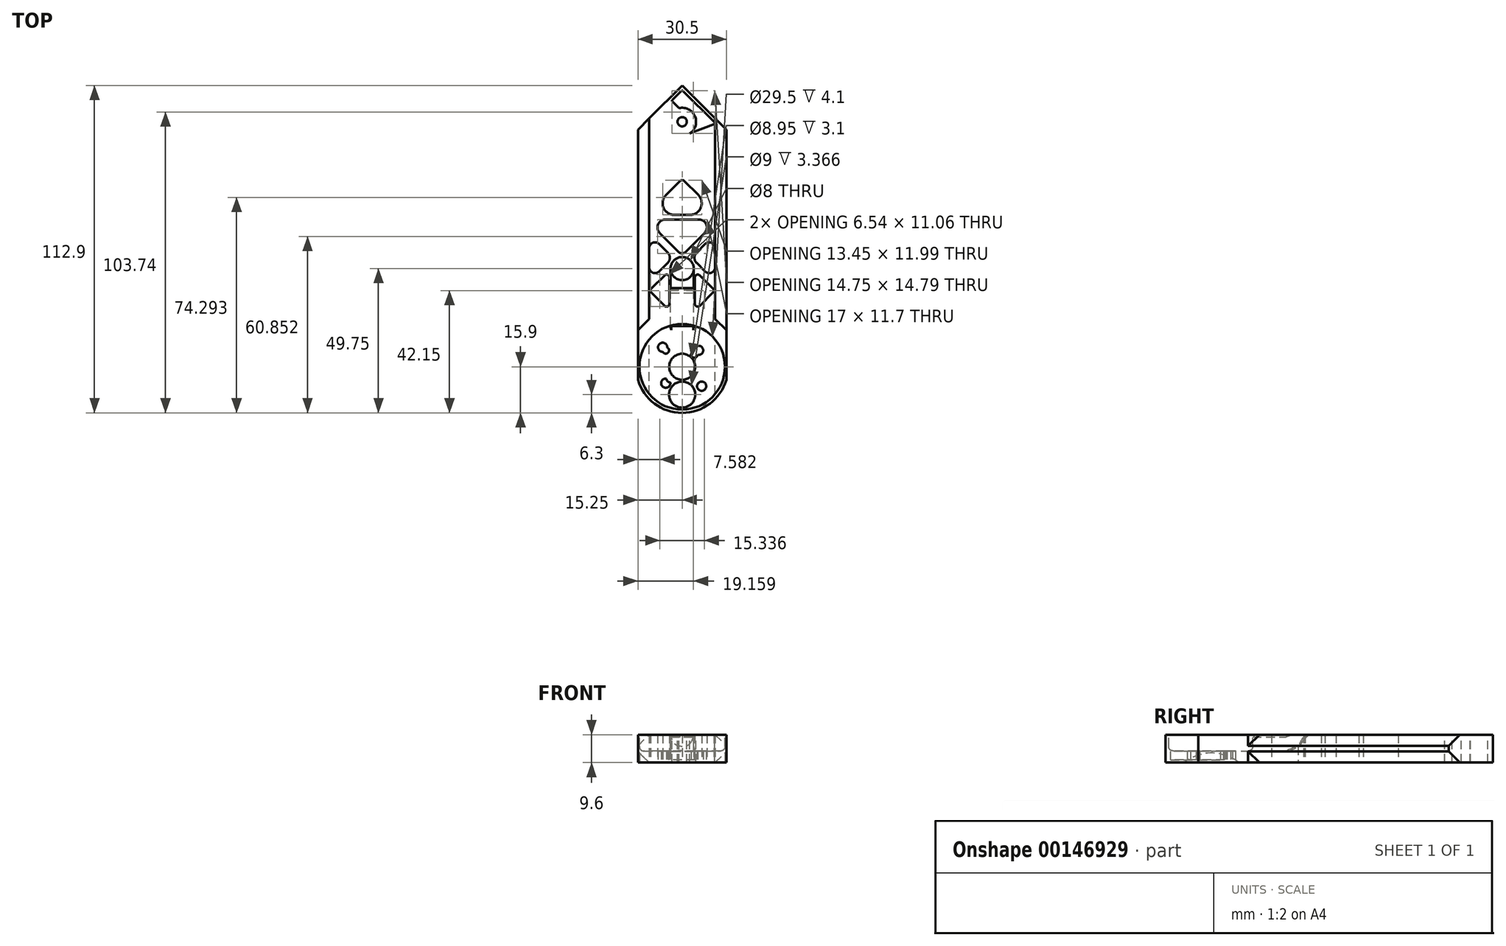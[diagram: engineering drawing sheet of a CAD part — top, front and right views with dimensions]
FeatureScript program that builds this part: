
annotation { "Feature Type Name" : "Feature", "Feature Type Description" : "" }
export const myFeature = defineFeature(function(context is Context, id is Id, definition is map)
    precondition{}
    {
        {
            var Q0;
            Q0=qCreatedBy(makeId("Top.planeOp"),FACE);
            var sketch = newSketch(context, id + "F0", { "sketchPlane" : qUnion([Q0])});
            skLineSegment(sketch, "E0", {"start": v(0, 0) * mm, "end": v(-10, 0) * mm});
            skLineSegment(sketch, "E1", {"start": v(-7.84, 7.84) * mm, "end": v(0, 0) * mm});
            skLineSegment(sketch, "E2", {"start": v(-6.78, -6.78) * mm, "end": v(0, 0) * mm});
            skLineSegment(sketch, "E3", {"start": v(0, 0) * mm, "end": v(-5.66, -5.66) * mm});
            skCircle(sketch, "E4", {"center": v(-5.66, -5.66) * mm, "radius": 1.59 * mm});
            skLineSegment(sketch, "E5", {"start": v(0, 0) * mm, "end": v(-6.72, 6.72) * mm});
            skCircle(sketch, "E6", {"center": v(-6.72, 6.72) * mm, "radius": 1.59 * mm});
            skLineSegment(sketch, "E7", {"start": v(0, 0) * mm, "end": v(-5.66, 5.66) * mm});
            skCircle(sketch, "E8", {"center": v(-5.66, 5.66) * mm, "radius": 1.13 * mm});
            skLineSegment(sketch, "E9.MirrorCS", {"start": v(7.84, -7.84) * mm, "end": v(0, 0) * mm});
            skLineSegment(sketch, "E10.MirrorCS", {"start": v(0, 0) * mm, "end": v(5.66, -5.66) * mm});
            skCircle(sketch, "E11.MirrorC", {"center": v(6.72, -6.72) * mm, "radius": 1.59 * mm});
            skCircle(sketch, "E12.MirrorC", {"center": v(5.66, -5.66) * mm, "radius": 1.13 * mm});
            skLineSegment(sketch, "E13.MirrorCS", {"start": v(0, 0) * mm, "end": v(6.72, -6.72) * mm});
            skCircle(sketch, "E14.MirrorC", {"center": v(5.66, 5.66) * mm, "radius": 1.59 * mm});
            skLineSegment(sketch, "E15.MirrorCS", {"start": v(0, 0) * mm, "end": v(5.66, 5.66) * mm});
            skLineSegment(sketch, "E16.MirrorCS", {"start": v(6.78, 6.78) * mm, "end": v(0, 0) * mm});
            skPoint(sketch, "E17.MirrorCS.start.orphan", {"position": v(0, 10) * mm});
            skPoint(sketch, "E18.orphan", {"position": v(10, 10) * mm});
            skPoint(sketch, "E19.orphan", {"position": v(10, -10) * mm});
            skPoint(sketch, "E20.orphan", {"position": v(-10, 10) * mm});
            skPoint(sketch, "E21.orphan", {"position": v(-10, -10) * mm});
            skCircle(sketch, "E22", {"center": v(-4.24, -4.24) * mm, "radius": 1.13 * mm});
            skCircle(sketch, "E23", {"center": v(4.24, 4.24) * mm, "radius": 1.13 * mm});
            skSolve(sketch);
        }
        {
            var Q0;
            Q0=qCreatedBy(makeId("Front.planeOp"),FACE);
            var sketch = newSketch(context, id + "F1", { "sketchPlane" : qUnion([Q0])});
            skLineSegment(sketch, "E24", {"start": v(0, 0) * mm, "end": v(11.35, 0) * mm});
            skLineSegment(sketch, "E25", {"start": v(-11.35, 0) * mm, "end": v(0, 0) * mm});
            skLineSegment(sketch, "E26", {"start": v(0, 0) * mm, "end": v(0, 3.8) * mm});
            skLineSegment(sketch, "E27", {"start": v(0, 3.8) * mm, "end": v(15.25, 3.8) * mm});
            skLineSegment(sketch, "E28", {"start": v(-15.25, 3.8) * mm, "end": v(0, 3.8) * mm});
            skPoint(sketch, "E29.orphan", {"position": v(15.25, 0) * mm});
            skPoint(sketch, "E30.orphan", {"position": v(-15.25, 0) * mm});
            skLineSegment(sketch, "E31", {"start": v(-15.25, 3.8) * mm, "end": v(-11.35, 0) * mm});
            skLineSegment(sketch, "E32", {"start": v(15.25, 3.8) * mm, "end": v(11.35, 0) * mm});
            skLineSegment(sketch, "E33", {"start": v(15.25, 3.8) * mm, "end": v(15.25, 5.8) * mm});
            skLineSegment(sketch, "E34", {"start": v(15.25, 5.8) * mm, "end": v(11.35, 9.6) * mm});
            skLineSegment(sketch, "E35", {"start": v(11.35, 9.6) * mm, "end": v(0, 9.6) * mm});
            skLineSegment(sketch, "E36.MirrorCS", {"start": v(-11.35, 9.6) * mm, "end": v(0, 9.6) * mm});
            skLineSegment(sketch, "E37.MirrorCS", {"start": v(-15.25, 5.8) * mm, "end": v(-11.35, 9.6) * mm});
            skLineSegment(sketch, "E38.MirrorCS", {"start": v(-15.25, 3.8) * mm, "end": v(-15.25, 5.8) * mm});
            skSolve(sketch);
        }
        {
            var Q0;
            Q0=qSketchRegion(id+"F1",true);
            extrude(context, id + "F2", {"entities" : qUnion([Q0]), "depth" : 16.3 * mm, "hasSecondDirection" : true, "secondDirectionOppositeDirection" : true, "secondDirectionDepth" : 97 * mm});
        }
        {
            var Q0;
            Q0=qCreatedBy(makeId("Top.planeOp"),FACE);
            cPlane(context, id + "F3", {"entities" : qUnion([Q0]), "cplaneType" : CPlaneType.OFFSET, "offset" : 16 * mm, "width" : 150 * mm, "height" : 150 * mm});
        }
        {
            var Q0;
            Q0=makeQuery(id+"F2.opExtrude","SWEPT_FACE",FACE,{"disambiguationData":[OSD([sQuery(id+"F1.wireOp",EDGE,"E35"),sQuery(id+"F1.wireOp",EDGE,"E36.MirrorCS")])]});
            var sketch = newSketch(context, id + "F4", { "sketchPlane" : qUnion([Q0])});
            skCircle(sketch, "E39", {"center": v(0, 0) * mm, "radius": 14.75 * mm});
            skLineSegment(sketch, "E40", {"start": v(14.75, 0) * mm, "end": v(-14.75, 0) * mm});
            skSolve(sketch);
        }
        {
            var Q0;
            {var subQ0=sQuery(id+"F4.wireOp",EDGE,"E39");var subQ1=makeQuery(id+"F2.opExtrude","SWEPT_EDGE",EDGE,{"disambiguationData":[OSD([sQuery(id+"F1.wireOp",EDGE,"E34"),sQuery(id+"F1.wireOp",EDGE,"E35")])]});var subQ2=makeQuery(id+"F4.imprint","INTERSECT",VERTEX,{"disambiguationData":[OD(0.0)],"derivedFrom":[subQ1,subQ0]});Q0=makeQuery(id+"F4.imprint","IMPRINT",FACE,{"disambiguationData":[TD([[makeQuery(id+"F4.imprint","IMPRINT",EDGE,{"disambiguationData":[TD([[subQ2,-1.0]])],"derivedFrom":subQ0}),1.0]])]});}
            var Q1;
            {var subQ0=sQuery(id+"F4.wireOp",EDGE,"E39");var subQ1=makeQuery(id+"F2.opExtrude","SWEPT_EDGE",EDGE,{"disambiguationData":[OSD([sQuery(id+"F1.wireOp",EDGE,"E36.MirrorCS"),sQuery(id+"F1.wireOp",EDGE,"E37.MirrorCS")])]});var subQ2=makeQuery(id+"F4.imprint","INTERSECT",VERTEX,{"disambiguationData":[OD(1.0)],"derivedFrom":[subQ1,subQ0]});Q1=makeQuery(id+"F4.imprint","IMPRINT",FACE,{"disambiguationData":[TD([[makeQuery(id+"F4.imprint","IMPRINT",EDGE,{"disambiguationData":[TD([[subQ2,-1.0]])],"derivedFrom":subQ0}),1.0]])]});}
            var Q2;
            {var subQ0=sQuery(id+"F4.wireOp",EDGE,"E40");var subQ1=sQuery(id+"F4.wireOp",EDGE,"E39");var subQ2=makeQuery(id+"F4.imprint","INTERSECT",VERTEX,{"disambiguationData":[OD(1.0)],"derivedFrom":[subQ1,subQ0]});Q2=makeQuery(id+"F4.imprint","IMPRINT",FACE,{"disambiguationData":[TD([[makeQuery(id+"F4.imprint","IMPRINT",EDGE,{"disambiguationData":[TD([[subQ2,-1.0]])],"derivedFrom":subQ1}),1.0]])]});}
            var Q3;
            {var subQ0=sQuery(id+"F4.wireOp",EDGE,"E40");var subQ1=sQuery(id+"F4.wireOp",EDGE,"E39");var subQ2=makeQuery(id+"F4.imprint","INTERSECT",VERTEX,{"disambiguationData":[OD(1.0)],"derivedFrom":[subQ1,subQ0]});Q3=makeQuery(id+"F4.imprint","IMPRINT",FACE,{"disambiguationData":[TD([[makeQuery(id+"F4.imprint","IMPRINT",EDGE,{"disambiguationData":[TD([[subQ2,1.0]])],"derivedFrom":subQ1}),1.0]])]});}
            var Q4;
            {var subQ0=sQuery(id+"F4.wireOp",EDGE,"E40");var subQ1=sQuery(id+"F4.wireOp",EDGE,"E39");var subQ2=makeQuery(id+"F4.imprint","INTERSECT",VERTEX,{"disambiguationData":[OD(0.0)],"derivedFrom":[subQ1,subQ0]});Q4=makeQuery(id+"F4.imprint","IMPRINT",FACE,{"disambiguationData":[TD([[makeQuery(id+"F4.imprint","IMPRINT",EDGE,{"disambiguationData":[TD([[subQ2,-1.0]])],"derivedFrom":subQ1}),1.0]])]});}
            var Q5;
            {var subQ0=sQuery(id+"F4.wireOp",EDGE,"E40");var subQ1=sQuery(id+"F4.wireOp",EDGE,"E39");var subQ2=makeQuery(id+"F4.imprint","INTERSECT",VERTEX,{"disambiguationData":[OD(0.0)],"derivedFrom":[subQ1,subQ0]});Q5=makeQuery(id+"F4.imprint","IMPRINT",FACE,{"disambiguationData":[TD([[makeQuery(id+"F4.imprint","IMPRINT",EDGE,{"disambiguationData":[TD([[subQ2,1.0]])],"derivedFrom":subQ1}),1.0]])]});}
            extrude(context, id + "F5", {"entities" : qUnion([Q0, Q1, Q2, Q3, Q4, Q5]), "operationType" : NewBodyOperationType.REMOVE, "oppositeDirection" : true, "depth" : 5.6 * mm});
        }
        {
            var Q0;
            {var subQ5=sQuery(id+"F0.wireOp",EDGE,"E1");Q0=makeQuery(id+"F0.imprint","IMPRINT",FACE,{"disambiguationData":[TD([[makeQuery(id+"F0.imprint","IMPRINT",EDGE,{"derivedFrom":subQ5}),-1.0]])]});}
            var Q1;
            {var subQ3=sQuery(id+"F0.wireOp",EDGE,"E1");Q1=makeQuery(id+"F0.imprint","IMPRINT",FACE,{"disambiguationData":[TD([[makeQuery(id+"F0.imprint","IMPRINT",EDGE,{"derivedFrom":subQ3}),1.0]])]});}
            var Q2;
            {var subQ5=sQuery(id+"F0.wireOp",EDGE,"E2");Q2=makeQuery(id+"F0.imprint","IMPRINT",FACE,{"disambiguationData":[TD([[makeQuery(id+"F0.imprint","IMPRINT",EDGE,{"derivedFrom":subQ5}),1.0]])]});}
            var Q3;
            {var subQ5=sQuery(id+"F0.wireOp",EDGE,"E2");Q3=makeQuery(id+"F0.imprint","IMPRINT",FACE,{"disambiguationData":[TD([[makeQuery(id+"F0.imprint","IMPRINT",EDGE,{"derivedFrom":subQ5}),-1.0]])]});}
            var Q4;
            {var subQ0=sQuery(id+"F0.wireOp",EDGE,"E22");var subQ3=sQuery(id+"F0.wireOp",EDGE,"E3");var subQ4=makeQuery(id+"F0.imprint","INTERSECT",VERTEX,{"disambiguationData":[OD(0.0)],"derivedFrom":[subQ3,subQ0]});Q4=makeQuery(id+"F0.imprint","IMPRINT",FACE,{"disambiguationData":[TD([[makeQuery(id+"F0.imprint","IMPRINT",EDGE,{"disambiguationData":[TD([[subQ4,-1.0]])],"derivedFrom":subQ3}),1.0]])]});}
            var Q5;
            {var subQ0=sQuery(id+"F0.wireOp",EDGE,"E22");var subQ3=sQuery(id+"F0.wireOp",EDGE,"E3");var subQ4=makeQuery(id+"F0.imprint","INTERSECT",VERTEX,{"disambiguationData":[OD(0.0)],"derivedFrom":[subQ3,subQ0]});Q5=makeQuery(id+"F0.imprint","IMPRINT",FACE,{"disambiguationData":[TD([[makeQuery(id+"F0.imprint","IMPRINT",EDGE,{"disambiguationData":[TD([[subQ4,-1.0]])],"derivedFrom":subQ3}),-1.0]])]});}
            var Q6;
            {var subQ1=sQuery(id+"F0.wireOp",EDGE,"E6");var subQ3=sQuery(id+"F0.wireOp",EDGE,"E8");var subQ5=makeQuery(id+"F0.imprint","INTERSECT",VERTEX,{"disambiguationData":[OD(0.0)],"derivedFrom":[subQ1,subQ3]});Q6=makeQuery(id+"F0.imprint","IMPRINT",FACE,{"disambiguationData":[TD([[makeQuery(id+"F0.imprint","IMPRINT",EDGE,{"disambiguationData":[TD([[subQ5,-1.0]])],"derivedFrom":subQ1}),-1.0]])]});}
            var Q7;
            {var subQ1=sQuery(id+"F0.wireOp",EDGE,"E6");var subQ3=sQuery(id+"F0.wireOp",EDGE,"E8");var subQ5=makeQuery(id+"F0.imprint","INTERSECT",VERTEX,{"disambiguationData":[OD(1.0)],"derivedFrom":[subQ1,subQ3]});Q7=makeQuery(id+"F0.imprint","IMPRINT",FACE,{"disambiguationData":[TD([[makeQuery(id+"F0.imprint","IMPRINT",EDGE,{"disambiguationData":[TD([[subQ5,1.0]])],"derivedFrom":subQ1}),-1.0]])]});}
            var Q8;
            {var subQ3=sQuery(id+"F0.wireOp",EDGE,"E9.MirrorCS");Q8=makeQuery(id+"F0.imprint","IMPRINT",FACE,{"disambiguationData":[TD([[makeQuery(id+"F0.imprint","IMPRINT",EDGE,{"derivedFrom":subQ3}),1.0]])]});}
            var Q9;
            {var subQ3=sQuery(id+"F0.wireOp",EDGE,"E9.MirrorCS");Q9=makeQuery(id+"F0.imprint","IMPRINT",FACE,{"disambiguationData":[TD([[makeQuery(id+"F0.imprint","IMPRINT",EDGE,{"derivedFrom":subQ3}),-1.0]])]});}
            var Q10;
            {var subQ1=sQuery(id+"F0.wireOp",EDGE,"E11.MirrorC");var subQ3=sQuery(id+"F0.wireOp",EDGE,"E12.MirrorC");var subQ5=makeQuery(id+"F0.imprint","INTERSECT",VERTEX,{"disambiguationData":[OD(0.0)],"derivedFrom":[subQ1,subQ3]});Q10=makeQuery(id+"F0.imprint","IMPRINT",FACE,{"disambiguationData":[TD([[makeQuery(id+"F0.imprint","IMPRINT",EDGE,{"disambiguationData":[TD([[subQ5,-1.0]])],"derivedFrom":subQ1}),1.0]])]});}
            var Q11;
            {var subQ1=sQuery(id+"F0.wireOp",EDGE,"E11.MirrorC");var subQ3=sQuery(id+"F0.wireOp",EDGE,"E12.MirrorC");var subQ5=makeQuery(id+"F0.imprint","INTERSECT",VERTEX,{"disambiguationData":[OD(1.0)],"derivedFrom":[subQ1,subQ3]});Q11=makeQuery(id+"F0.imprint","IMPRINT",FACE,{"disambiguationData":[TD([[makeQuery(id+"F0.imprint","IMPRINT",EDGE,{"disambiguationData":[TD([[subQ5,1.0]])],"derivedFrom":subQ1}),1.0]])]});}
            var Q12;
            {var subQ0=sQuery(id+"F0.wireOp",EDGE,"E23");var subQ1=sQuery(id+"F0.wireOp",EDGE,"E14.MirrorC");var subQ2=makeQuery(id+"F0.imprint","INTERSECT",VERTEX,{"disambiguationData":[OD(1.0)],"derivedFrom":[subQ1,subQ0]});Q12=makeQuery(id+"F0.imprint","IMPRINT",FACE,{"disambiguationData":[TD([[makeQuery(id+"F0.imprint","IMPRINT",EDGE,{"disambiguationData":[TD([[subQ2,1.0]])],"derivedFrom":subQ1}),1.0]])]});}
            var Q13;
            {var subQ1=sQuery(id+"F0.wireOp",EDGE,"E16.MirrorCS");var subQ5=makeQuery(id+"F0.imprint","IMPRINT",VERTEX,{"derivedFrom":subQ1});Q13=makeQuery(id+"F0.imprint","IMPRINT",FACE,{"disambiguationData":[TD([[makeQuery(id+"F0.imprint","IMPRINT",EDGE,{"disambiguationData":[TD([[subQ5,1.0]])],"derivedFrom":subQ1}),-1.0]])]});}
            var Q14;
            {var subQ1=sQuery(id+"F0.wireOp",EDGE,"E16.MirrorCS");var subQ5=makeQuery(id+"F0.imprint","IMPRINT",VERTEX,{"derivedFrom":subQ1});Q14=makeQuery(id+"F0.imprint","IMPRINT",FACE,{"disambiguationData":[TD([[makeQuery(id+"F0.imprint","IMPRINT",EDGE,{"disambiguationData":[TD([[subQ5,1.0]])],"derivedFrom":subQ1}),1.0]])]});}
            var Q15;
            {var subQ1=sQuery(id+"F0.wireOp",EDGE,"E3");var subQ3=sQuery(id+"F0.wireOp",EDGE,"E4");var subQ5=makeQuery(id+"F0.imprint","INTERSECT",VERTEX,{"derivedFrom":[subQ1,subQ3]});Q15=makeQuery(id+"F0.imprint","IMPRINT",FACE,{"disambiguationData":[TD([[makeQuery(id+"F0.imprint","IMPRINT",EDGE,{"disambiguationData":[TD([[subQ5,-1.0]])],"derivedFrom":subQ1}),1.0]])]});}
            var Q16;
            {var subQ1=sQuery(id+"F0.wireOp",EDGE,"E3");var subQ3=sQuery(id+"F0.wireOp",EDGE,"E4");var subQ5=makeQuery(id+"F0.imprint","INTERSECT",VERTEX,{"derivedFrom":[subQ1,subQ3]});Q16=makeQuery(id+"F0.imprint","IMPRINT",FACE,{"disambiguationData":[TD([[makeQuery(id+"F0.imprint","IMPRINT",EDGE,{"disambiguationData":[TD([[subQ5,-1.0]])],"derivedFrom":subQ1}),-1.0]])]});}
            var Q17;
            {var subQ0=sQuery(id+"F0.wireOp",EDGE,"E13.MirrorCS");var subQ3=makeQuery(id+"F0.imprint","IMPRINT",VERTEX,{"derivedFrom":subQ0});Q17=makeQuery(id+"F0.imprint","IMPRINT",FACE,{"disambiguationData":[TD([[makeQuery(id+"F0.imprint","IMPRINT",EDGE,{"disambiguationData":[TD([[subQ3,1.0]])],"derivedFrom":subQ0}),1.0]])]});}
            var Q18;
            {var subQ0=sQuery(id+"F0.wireOp",EDGE,"E23");var subQ3=sQuery(id+"F0.wireOp",EDGE,"E14.MirrorC");var subQ4=makeQuery(id+"F0.imprint","INTERSECT",VERTEX,{"disambiguationData":[OD(1.0)],"derivedFrom":[subQ3,subQ0]});Q18=makeQuery(id+"F0.imprint","IMPRINT",FACE,{"disambiguationData":[TD([[makeQuery(id+"F0.imprint","IMPRINT",EDGE,{"disambiguationData":[TD([[subQ4,1.0]])],"derivedFrom":subQ3}),-1.0]])]});}
            var Q19;
            {var subQ0=sQuery(id+"F0.wireOp",EDGE,"E23");var subQ1=sQuery(id+"F0.wireOp",EDGE,"E14.MirrorC");var subQ2=makeQuery(id+"F0.imprint","INTERSECT",VERTEX,{"disambiguationData":[OD(0.0)],"derivedFrom":[subQ1,subQ0]});Q19=makeQuery(id+"F0.imprint","IMPRINT",FACE,{"disambiguationData":[TD([[makeQuery(id+"F0.imprint","IMPRINT",EDGE,{"disambiguationData":[TD([[subQ2,-1.0]])],"derivedFrom":subQ1}),1.0]])]});}
            var Q20;
            {var subQ0=sQuery(id+"F0.wireOp",EDGE,"E23");var subQ3=sQuery(id+"F0.wireOp",EDGE,"E14.MirrorC");var subQ4=makeQuery(id+"F0.imprint","INTERSECT",VERTEX,{"disambiguationData":[OD(0.0)],"derivedFrom":[subQ3,subQ0]});Q20=makeQuery(id+"F0.imprint","IMPRINT",FACE,{"disambiguationData":[TD([[makeQuery(id+"F0.imprint","IMPRINT",EDGE,{"disambiguationData":[TD([[subQ4,-1.0]])],"derivedFrom":subQ3}),-1.0]])]});}
            var Q21;
            {var subQ0=sQuery(id+"F0.wireOp",EDGE,"E13.MirrorCS");var subQ3=makeQuery(id+"F0.imprint","IMPRINT",VERTEX,{"derivedFrom":subQ0});Q21=makeQuery(id+"F0.imprint","IMPRINT",FACE,{"disambiguationData":[TD([[makeQuery(id+"F0.imprint","IMPRINT",EDGE,{"disambiguationData":[TD([[subQ3,1.0]])],"derivedFrom":subQ0}),-1.0]])]});}
            var Q22;
            {var subQ1=sQuery(id+"F0.wireOp",EDGE,"E5");var subQ5=sQuery(id+"F0.wireOp",EDGE,"E7");var subQ7=makeQuery(id+"F0.imprint","INTERSECT",VERTEX,{"derivedFrom":[subQ1,subQ5]});Q22=makeQuery(id+"F0.imprint","IMPRINT",FACE,{"disambiguationData":[TD([[makeQuery(id+"F0.imprint","IMPRINT",EDGE,{"disambiguationData":[TD([[subQ7,-1.0]])],"derivedFrom":subQ1}),1.0]])]});}
            var Q23;
            {var subQ1=sQuery(id+"F0.wireOp",EDGE,"E5");var subQ5=sQuery(id+"F0.wireOp",EDGE,"E7");var subQ7=makeQuery(id+"F0.imprint","INTERSECT",VERTEX,{"derivedFrom":[subQ1,subQ5]});Q23=makeQuery(id+"F0.imprint","IMPRINT",FACE,{"disambiguationData":[TD([[makeQuery(id+"F0.imprint","IMPRINT",EDGE,{"disambiguationData":[TD([[subQ7,-1.0]])],"derivedFrom":subQ1}),-1.0]])]});}
            extrude(context, id + "F6", {"entities" : qUnion([Q0, Q1, Q2, Q3, Q4, Q5, Q6, Q7, Q8, Q9, Q10, Q11, Q12, Q13, Q14, Q15, Q16, Q17, Q18, Q19, Q20, Q21, Q22, Q23]), "operationType" : NewBodyOperationType.REMOVE, "endBound" : BoundingType.THROUGH_ALL, "depth" : 5 * mm});
        }
        {
            var Q0;
            Q0=qCreatedBy(makeId("Top.planeOp"),FACE);
            var sketch = newSketch(context, id + "F7", { "sketchPlane" : qUnion([Q0])});
            skCircle(sketch, "E41", {"center": v(0, 0) * mm, "radius": 14.75 * mm});
            skArc(sketch, "E42", {"start": v(15.25, 4.5) * mm, "mid": v(0, 15.9) * mm, "end": v(-15.25, 4.5) * mm});
            skLineSegment(sketch, "E43", {"start": v(0, 0) * mm, "end": v(15.25, 0) * mm});
            skLineSegment(sketch, "E44", {"start": v(15.25, 0) * mm, "end": v(15.25, 4.5) * mm});
            skLineSegment(sketch, "E45.MirrorCS", {"start": v(15.25, 0) * mm, "end": v(15.25, -4.5) * mm});
            skLineSegment(sketch, "E46.MirrorCS", {"start": v(-15.25, 0) * mm, "end": v(-15.25, 4.5) * mm});
            skLineSegment(sketch, "E47.MirrorCS", {"start": v(-15.25, 0) * mm, "end": v(-15.25, -4.5) * mm});
            skArc(sketch, "E48.trimOffspring", {"start": v(-15.25, -4.5) * mm, "mid": v(0, -15.9) * mm, "end": v(15.25, -4.5) * mm});
            skSolve(sketch);
        }
        {
            var Q0;
            Q0=qSketchRegion(id+"F7",true);
            var Q1;
            Q1=makeQuery(id+"F2.opExtrude","SWEPT_FACE",FACE,{"disambiguationData":[OSD([sQuery(id+"F1.wireOp",EDGE,"E35"),sQuery(id+"F1.wireOp",EDGE,"E36.MirrorCS")])]});
            extrude(context, id + "F8", {"entities" : qUnion([Q0]), "operationType" : NewBodyOperationType.ADD, "endBound" : BoundingType.UP_TO_SURFACE, "endBoundEntityFace" : qUnion([Q1]), "depth" : 15.75 * mm});
        }
        {
            var Q0;
            Q0=qCreatedBy(id+"F3.planeOp",FACE);
            var sketch = newSketch(context, id + "F9", { "sketchPlane" : qUnion([Q0])});
            skCircle(sketch, "E49", {"center": v(0, 0) * mm, "radius": 15.9 * mm});
            skLineSegment(sketch, "E50", {"start": v(-15.9, 0) * mm, "end": v(-15.9, -16.3) * mm});
            skLineSegment(sketch, "E51.bottom", {"start": v(-15.9, -16.3) * mm, "end": v(15.9, -16.3) * mm});
            skLineSegment(sketch, "E51.top", {"start": v(-15.9, 0) * mm, "end": v(15.9, 0) * mm});
            skLineSegment(sketch, "E51.left", {"start": v(-15.9, -16.3) * mm, "end": v(-15.9, 0) * mm});
            skLineSegment(sketch, "E51.right", {"start": v(15.9, -16.3) * mm, "end": v(15.9, 0) * mm});
            skLineSegment(sketch, "E52", {"start": v(0, 0) * mm, "end": v(-3.75, 0) * mm});
            skLineSegment(sketch, "E53.bottom", {"start": v(-3.75, -16.3) * mm, "end": v(3.75, -16.3) * mm});
            skSolve(sketch);
        }
        {
            var Q0;
            {var subQ3=sQuery(id+"F9.wireOp",EDGE,"E51.left");Q0=makeQuery(id+"F9.imprint","IMPRINT",FACE,{"disambiguationData":[TD([[makeQuery(id+"F9.imprint","IMPRINT",EDGE,{"derivedFrom":subQ3}),-1.0]])]});}
            var Q1;
            {var subQ3=sQuery(id+"F9.wireOp",EDGE,"E51.left");Q1=makeQuery(id+"F9.imprint","IMPRINT",FACE,{"disambiguationData":[TD([[makeQuery(id+"F9.imprint","IMPRINT",EDGE,{"derivedFrom":subQ3}),-1.0]])]});}
            var Q2;
            {var subQ0=sQuery(id+"F9.wireOp",EDGE,"E51.right");Q2=makeQuery(id+"F9.imprint","IMPRINT",FACE,{"disambiguationData":[TD([[makeQuery(id+"F9.imprint","IMPRINT",EDGE,{"derivedFrom":subQ0}),1.0]])]});}
            extrude(context, id + "F10", {"entities" : qUnion([Q0, Q1, Q2]), "operationType" : NewBodyOperationType.REMOVE, "oppositeDirection" : true, "depth" : 25 * mm});
        }
        {
            var Q0;
            Q0=makeQuery(id+"F5.boolean.opBoolean","COPY",FACE,{"derivedFrom":makeQuery(id+"F5.opExtrude","CAP_FACE",FACE,{"disambiguationData":[OSD([sQuery(id+"F4.wireOp",EDGE,"E39")])],"isStart":false})});
            var sketch = newSketch(context, id + "F11", { "sketchPlane" : qUnion([Q0])});
            skCircle(sketch, "E54", {"center": v(0, 0) * mm, "radius": 4.47 * mm});
            skLineSegment(sketch, "E55", {"start": v(0, 0) * mm, "end": v(9.25, 0) * mm});
            skLineSegment(sketch, "E56", {"start": v(0, 0) * mm, "end": v(0, -9.6) * mm});
            skCircle(sketch, "E57", {"center": v(0, -9.6) * mm, "radius": 4.5 * mm});
            skLineSegment(sketch, "E58.MirrorCS", {"start": v(0, 0) * mm, "end": v(-9.25, 0) * mm});
            skSolve(sketch);
        }
        {
            var Q0;
            Q0=qSketchRegion(id+"F11",true);
            extrude(context, id + "F12", {"entities" : qUnion([Q0]), "operationType" : NewBodyOperationType.REMOVE, "oppositeDirection" : true, "depth" : 3.1 * mm});
        }
        {
            var Q0;
            Q0=qCreatedBy(makeId("Top.planeOp"),FACE);
            cPlane(context, id + "F13", {"entities" : qUnion([Q0]), "cplaneType" : CPlaneType.OFFSET, "offset" : 0 * mm, "width" : 150 * mm, "height" : 150 * mm});
        }
        {
            var Q0;
            Q0=qCreatedBy(makeId("Top.planeOp"),FACE);
            var sketch = newSketch(context, id + "F14", { "sketchPlane" : qUnion([Q0])});
            skLineSegment(sketch, "E59", {"start": v(0, 81.75) * mm, "end": v(15.25, 81.75) * mm});
            skLineSegment(sketch, "E60", {"start": v(15.25, 81.75) * mm, "end": v(0, 97) * mm});
            skLineSegment(sketch, "E61.MirrorCS", {"start": v(-15.25, 81.75) * mm, "end": v(0, 97) * mm});
            skLineSegment(sketch, "E62.MirrorCS", {"start": v(0, 81.75) * mm, "end": v(-15.25, 81.75) * mm});
            skLineSegment(sketch, "E63", {"start": v(-15.25, 81.75) * mm, "end": v(-15.25, 97) * mm});
            skLineSegment(sketch, "E64", {"start": v(-15.25, 97) * mm, "end": v(15.25, 97) * mm});
            skLineSegment(sketch, "E65", {"start": v(15.25, 97) * mm, "end": v(15.25, 81.75) * mm});
            skSolve(sketch);
        }
        {
            var Q0;
            Q0=makeQuery(id+"F14.imprint","IMPRINT",FACE,{"disambiguationData":[TD([[makeQuery(id+"F14.imprint","IMPRINT",EDGE,{"derivedFrom":sQuery(id+"F14.wireOp",EDGE,"E60")}),-1.0]])]});
            var Q1;
            {var subQ0=sQuery(id+"F14.wireOp",EDGE,"E61.MirrorCS");Q1=makeQuery(id+"F14.imprint","IMPRINT",FACE,{"disambiguationData":[TD([[makeQuery(id+"F14.imprint","IMPRINT",EDGE,{"derivedFrom":subQ0}),1.0]])]});}
            extrude(context, id + "F15", {"entities" : qUnion([Q0, Q1]), "operationType" : NewBodyOperationType.REMOVE, "depth" : 25 * mm});
        }
        {
            var Q0;
            {var subQ0=sQuery(id+"F1.wireOp",EDGE,"E38.MirrorCS");var subQ1=sQuery(id+"F1.wireOp",EDGE,"E37.MirrorCS");var subQ2=sQuery(id+"F1.wireOp",EDGE,"E36.MirrorCS");var subQ3=sQuery(id+"F1.wireOp",EDGE,"E35");var subQ4=sQuery(id+"F1.wireOp",EDGE,"E34");var subQ5=sQuery(id+"F1.wireOp",EDGE,"E33");var subQ6=sQuery(id+"F1.wireOp",EDGE,"E32");var subQ7=sQuery(id+"F1.wireOp",EDGE,"E31");var subQ8=sQuery(id+"F1.wireOp",EDGE,"E25");var subQ9=sQuery(id+"F1.wireOp",EDGE,"E24");var subQ13=makeQuery(id+"F2.opExtrude","SWEPT_FACE",FACE,{"disambiguationData":[OSD([subQ3,subQ2])]});Q0=makeQuery(id+"F8.boolean.opBoolean","MERGE",FACE,{"derivedFrom":[makeQuery(id+"F5.boolean.opBoolean","SPLIT",FACE,{"disambiguationData":[TD([makeQuery(id+"F2.opExtrude","CAP_FACE",FACE,{"disambiguationData":[OSD([subQ9,subQ8,subQ7,subQ6,subQ5,subQ4,subQ3,subQ2,subQ1,subQ0])],"isStart":true})])],"derivedFrom":subQ13}),makeQuery(id+"F5.boolean.opBoolean","SPLIT",FACE,{"disambiguationData":[TD([makeQuery(id+"F2.opExtrude","CAP_FACE",FACE,{"disambiguationData":[OSD([subQ9,subQ8,subQ7,subQ6,subQ5,subQ4,subQ3,subQ2,subQ1,subQ0])],"isStart":false})])],"derivedFrom":subQ13}),makeQuery(id+"F8.opExtrude","CAP_FACE",FACE,{"disambiguationData":[OSD([sQuery(id+"F7.wireOp",EDGE,"E41"),sQuery(id+"F7.wireOp",EDGE,"E42")])],"isStart":false})]});}
            var sketch = newSketch(context, id + "F16", { "sketchPlane" : qUnion([Q0])});
            skLineSegment(sketch, "E66", {"start": v(0, 97) * mm, "end": v(0, 84.5) * mm});
            skCircle(sketch, "E67", {"center": v(0, 84.5) * mm, "radius": 1.6 * mm});
            skLineSegment(sketch, "E68.0", {"start": v(11.17, 84.23) * mm, "end": v(0.28, 95.12) * mm});
            skLineSegment(sketch, "E68.1", {"start": v(-3.35, 92.05) * mm, "end": v(-0.28, 95.12) * mm});
            skPoint(sketch, "E69.visualSharp", {"position": v(0, 95.4) * mm});
            skArc(sketch, "E69.filletArc", {"start": v(0.28, 95.12) * mm, "mid": v(0, 95.23) * mm, "end": v(-0.28, 95.12) * mm});
            skCircle(sketch, "E70", {"center": v(0, 84.5) * mm, "radius": 4.8 * mm});
            skLineSegment(sketch, "E71.trimOffspring", {"start": v(-1.05, 89.18) * mm, "end": v(-3.35, 91.48) * mm});
            skLineSegment(sketch, "E72.trimOffspring", {"start": v(2.57, 80.44) * mm, "end": v(11.02, 83.57) * mm});
            skPoint(sketch, "E73.visualSharp", {"position": v(-3.63, 91.77) * mm});
            skArc(sketch, "E73.filletArc", {"start": v(-3.35, 92.05) * mm, "mid": v(-3.47, 91.77) * mm, "end": v(-3.35, 91.48) * mm});
            skPoint(sketch, "E74.visualSharp", {"position": v(11.6, 83.8) * mm});
            skArc(sketch, "E74.filletArc", {"start": v(11.02, 83.57) * mm, "mid": v(11.28, 83.86) * mm, "end": v(11.17, 84.23) * mm});
            skSolve(sketch);
        }
        {
            var Q0;
            {var subQ4=sQuery(id+"F16.wireOp",EDGE,"E68.0");Q0=makeQuery(id+"F16.imprint","IMPRINT",FACE,{"disambiguationData":[TD([[makeQuery(id+"F16.imprint","IMPRINT",EDGE,{"derivedFrom":subQ4}),1.0]])]});}
            var Q1;
            {var subQ4=sQuery(id+"F16.wireOp",EDGE,"E68.1");Q1=makeQuery(id+"F16.imprint","IMPRINT",FACE,{"disambiguationData":[TD([[makeQuery(id+"F16.imprint","IMPRINT",EDGE,{"derivedFrom":subQ4}),-1.0]])]});}
            var Q2;
            Q2=makeQuery(id+"F16.imprint","IMPRINT",FACE,{"disambiguationData":[TD([[makeQuery(id+"F16.imprint","IMPRINT",EDGE,{"derivedFrom":sQuery(id+"F16.wireOp",EDGE,"E67")}),1.0]])]});
            extrude(context, id + "F17", {"entities" : qUnion([Q0, Q1, Q2]), "operationType" : NewBodyOperationType.REMOVE, "oppositeDirection" : true, "depth" : 25 * mm});
        }
        {
            var Q0;
            Q0=qCreatedBy(makeId("Front.planeOp"),FACE);
            cPlane(context, id + "F18", {"entities" : qUnion([Q0]), "cplaneType" : CPlaneType.OFFSET, "offset" : 14 * mm, "oppositeDirection" : true, "width" : 150 * mm, "height" : 150 * mm});
        }
        {
            var Q0;
            Q0=qCreatedBy(id+"F18.planeOp",FACE);
            var sketch = newSketch(context, id + "F19", { "sketchPlane" : qUnion([Q0])});
            skLineSegment(sketch, "E75", {"start": v(4, 3.9) * mm, "end": v(4, 8.8) * mm});
            skLineSegment(sketch, "E76.bottom", {"start": v(4, 8.8) * mm, "end": v(-4, 8.8) * mm});
            skLineSegment(sketch, "E76.left", {"start": v(4, 8.8) * mm, "end": v(4, 4.4) * mm});
            skLineSegment(sketch, "E76.right", {"start": v(-4, 8.8) * mm, "end": v(-4, 4.4) * mm});
            skLineSegment(sketch, "E77", {"start": v(0, 0) * mm, "end": v(0, 3.9) * mm});
            skLineSegment(sketch, "E78", {"start": v(0, 3.9) * mm, "end": v(3.5, 3.9) * mm});
            skLineSegment(sketch, "E79", {"start": v(0, 3.9) * mm, "end": v(-3.5, 3.9) * mm});
            skPoint(sketch, "E80.orphan", {"position": v(-4, 0) * mm});
            skPoint(sketch, "E76.top.start.orphan", {"position": v(4, 0) * mm});
            skPoint(sketch, "E81.visualSharp", {"position": v(4, 3.9) * mm});
            skArc(sketch, "E81.filletArc", {"start": v(3.5, 3.9) * mm, "mid": v(3.85, 4.05) * mm, "end": v(4, 4.4) * mm});
            skPoint(sketch, "E82.visualSharp", {"position": v(-4, 3.9) * mm});
            skArc(sketch, "E82.filletArc", {"start": v(-4, 4.4) * mm, "mid": v(-3.85, 4.05) * mm, "end": v(-3.5, 3.9) * mm});
            skSolve(sketch);
        }
        {
            var Q0;
            Q0=qCreatedBy(makeId("Right.planeOp"),FACE);
            var sketch = newSketch(context, id + "F20", { "sketchPlane" : qUnion([Q0])});
            skLineSegment(sketch, "E83", {"start": v(0, 0) * mm, "end": v(14.4, 0) * mm});
            skLineSegment(sketch, "E84", {"start": v(14.4, 0) * mm, "end": v(14.4, 3.9) * mm});
            skLineSegment(sketch, "E85", {"start": v(14.4, 3.9) * mm, "end": v(26.4, 3.9) * mm});
            skLineSegment(sketch, "E86", {"start": v(26.4, 3.9) * mm, "end": v(35, 3.9) * mm});
            skLineSegment(sketch, "E87", {"start": v(35, 3.9) * mm, "end": v(35, 9.5) * mm});
            skFitSpline(sketch, "E88", {"points": [v(26.4, 3.9) * mm, v(29.4, 5.26) * mm, v(31.06, 6.75) * mm, v(32.22, 8.3) * mm, v(35, 9.5) * mm], "startDerivative": vector(11.47, 4.47) * mm, "endDerivative": vector(11.77, 3.66) * mm});
            skLineSegment(sketch, "E89", {"start": v(35, 9.5) * mm, "end": v(36.63, 9.83) * mm});
            skSolve(sketch);
        }
        {
            var Q0;
            Q0=makeQuery(id+"F19.imprint","IMPRINT",FACE,{"disambiguationData":[TD([[makeQuery(id+"F19.imprint","IMPRINT",EDGE,{"derivedFrom":sQuery(id+"F19.wireOp",EDGE,"E76.bottom")}),1.0]])]});
            var Q1;
            Q1=sQuery(id+"F20.wireOp",EDGE,"E88");
            var Q2;
            Q2=sQuery(id+"F20.wireOp",EDGE,"E85");
            var Q3;
            Q3=sQuery(id+"F20.wireOp",EDGE,"E89");
            sweep(context, id + "F21", {"operationType" : NewBodyOperationType.REMOVE, "profiles" : qUnion([Q0]), "path" : qUnion([Q1, Q2, Q3])});
        }
        {
            var Q0;
            Q0=qCreatedBy(id+"F13.planeOp",FACE);
            var sketch = newSketch(context, id + "F22", { "sketchPlane" : qUnion([Q0])});
            skLineSegment(sketch, "E90", {"start": v(0, 0) * mm, "end": v(0, 37.6) * mm});
            skLineSegment(sketch, "E91", {"start": v(-11.35, 37.6) * mm, "end": v(0, 37.6) * mm});
            skLineSegment(sketch, "E92", {"start": v(-11.35, 37.6) * mm, "end": v(-11.35, 34.28) * mm});
            skLineSegment(sketch, "E93", {"start": v(-11.35, 37.6) * mm, "end": v(-11.35, 40.92) * mm});
            skLineSegment(sketch, "E94", {"start": v(-4.97, 39.37) * mm, "end": v(-7.94, 42.34) * mm});
            skLineSegment(sketch, "E95", {"start": v(-4.97, 35.83) * mm, "end": v(-7.94, 32.86) * mm});
            skPoint(sketch, "E96.visualSharp", {"position": v(-11.35, 29.45) * mm});
            skPoint(sketch, "E97.visualSharp", {"position": v(-3.2, 37.6) * mm});
            skLineSegment(sketch, "E97.filletArc", {"start": v(-3.2, 37.6) * mm, "end": v(-3.2, 37.6) * mm});
            skPoint(sketch, "E98.visualSharp", {"position": v(-11.35, 45.75) * mm});
            skLineSegment(sketch, "E99.MirrorCS", {"start": v(3.2, 37.6) * mm, "end": v(3.2, 37.6) * mm});
            skPoint(sketch, "E100.MirrorP", {"position": v(11.35, 29.45) * mm});
            skLineSegment(sketch, "E101.MirrorCS", {"start": v(11.35, 37.6) * mm, "end": v(0, 37.6) * mm});
            skLineSegment(sketch, "E102.MirrorCS", {"start": v(4.97, 35.83) * mm, "end": v(7.94, 32.86) * mm});
            skLineSegment(sketch, "E103.MirrorCS", {"start": v(11.35, 37.6) * mm, "end": v(11.35, 34.28) * mm});
            skLineSegment(sketch, "E104.MirrorCS", {"start": v(11.35, 37.6) * mm, "end": v(11.35, 40.92) * mm});
            skPoint(sketch, "E105.MirrorP", {"position": v(11.35, 45.75) * mm});
            skLineSegment(sketch, "E106.MirrorCS", {"start": v(4.97, 39.37) * mm, "end": v(7.94, 42.34) * mm});
            skLineSegment(sketch, "E107", {"start": v(1.2, 39.6) * mm, "end": v(7.7, 46.1) * mm});
            skLineSegment(sketch, "E108", {"start": v(5.76, 50.8) * mm, "end": v(0, 50.8) * mm});
            skLineSegment(sketch, "E109", {"start": v(0, 50.8) * mm, "end": v(0, 52.4) * mm});
            skLineSegment(sketch, "E110", {"start": v(0, 52.4) * mm, "end": v(2.74, 52.4) * mm});
            skLineSegment(sketch, "E111", {"start": v(5.57, 59.23) * mm, "end": v(0.7, 64.1) * mm});
            skPoint(sketch, "E112.visualSharp", {"position": v(12.4, 52.4) * mm});
            skArc(sketch, "E112.filletArc", {"start": v(2.74, 52.4) * mm, "mid": v(6.44, 54.87) * mm, "end": v(5.57, 59.23) * mm});
            skPoint(sketch, "E113.visualSharp", {"position": v(12.4, 50.8) * mm});
            skArc(sketch, "E113.filletArc", {"start": v(7.7, 46.1) * mm, "mid": v(8.3, 49.1) * mm, "end": v(5.76, 50.8) * mm});
            skLineSegment(sketch, "E114.MirrorCS", {"start": v(-5.57, 59.23) * mm, "end": v(-0.7, 64.1) * mm});
            skLineSegment(sketch, "E115.MirrorCS", {"start": v(-5.76, 50.8) * mm, "end": v(0, 50.8) * mm});
            skLineSegment(sketch, "E116.MirrorCS", {"start": v(0, 52.4) * mm, "end": v(-2.74, 52.4) * mm});
            skArc(sketch, "E117.MirrorCS", {"start": v(-2.74, 52.4) * mm, "mid": v(-6.44, 54.87) * mm, "end": v(-5.57, 59.23) * mm});
            skArc(sketch, "E118.MirrorCS", {"start": v(-7.7, 46.1) * mm, "mid": v(-8.3, 49.1) * mm, "end": v(-5.76, 50.8) * mm});
            skLineSegment(sketch, "E119.MirrorCS", {"start": v(-1.2, 39.6) * mm, "end": v(-7.7, 46.1) * mm});
            skPoint(sketch, "E120.visualSharp", {"position": v(0, 64.8) * mm});
            skArc(sketch, "E120.filletArc", {"start": v(0.7, 64.1) * mm, "mid": v(0, 64.39) * mm, "end": v(-0.7, 64.1) * mm});
            skPoint(sketch, "E121.visualSharp", {"position": v(0, 38.4) * mm});
            skArc(sketch, "E121.filletArc", {"start": v(-1.2, 39.6) * mm, "mid": v(0, 39.1) * mm, "end": v(1.2, 39.6) * mm});
            skArc(sketch, "E122.filletArc", {"start": v(-7.94, 42.34) * mm, "mid": v(-10.12, 42.77) * mm, "end": v(-11.35, 40.92) * mm});
            skArc(sketch, "E123.filletArc", {"start": v(-11.35, 34.28) * mm, "mid": v(-10.12, 32.43) * mm, "end": v(-7.94, 32.86) * mm});
            skArc(sketch, "E124.filletArc", {"start": v(-4.97, 35.83) * mm, "mid": v(-4.24, 37.6) * mm, "end": v(-4.97, 39.37) * mm});
            skArc(sketch, "E125.filletArc", {"start": v(11.35, 40.92) * mm, "mid": v(10.12, 42.77) * mm, "end": v(7.94, 42.34) * mm});
            skArc(sketch, "E126.filletArc", {"start": v(4.97, 39.37) * mm, "mid": v(4.24, 37.6) * mm, "end": v(4.97, 35.83) * mm});
            skLineSegment(sketch, "E127", {"start": v(-11.35, 26.25) * mm, "end": v(-4.4, 26.25) * mm});
            skLineSegment(sketch, "E128", {"start": v(-4.4, 26.25) * mm, "end": v(-4.4, 30.79) * mm});
            skLineSegment(sketch, "E129", {"start": v(-6.1, 31.5) * mm, "end": v(-10.64, 26.96) * mm});
            skLineSegment(sketch, "E130.MirrorCS", {"start": v(-4.4, 26.25) * mm, "end": v(-4.4, 21.71) * mm});
            skLineSegment(sketch, "E131.MirrorCS", {"start": v(-6.1, 21) * mm, "end": v(-10.64, 25.54) * mm});
            skPoint(sketch, "E132.visualSharp", {"position": v(-4.4, 33.2) * mm});
            skArc(sketch, "E132.filletArc", {"start": v(-4.4, 30.79) * mm, "mid": v(-5.02, 31.7) * mm, "end": v(-6.1, 31.5) * mm});
            skPoint(sketch, "E133.visualSharp", {"position": v(-4.4, 19.3) * mm});
            skArc(sketch, "E133.filletArc", {"start": v(-6.1, 21) * mm, "mid": v(-5.02, 20.8) * mm, "end": v(-4.4, 21.71) * mm});
            skPoint(sketch, "E134.visualSharp", {"position": v(-11.35, 26.25) * mm});
            skArc(sketch, "E134.filletArc", {"start": v(-10.64, 26.96) * mm, "mid": v(-10.94, 26.25) * mm, "end": v(-10.64, 25.54) * mm});
            skLineSegment(sketch, "E135.MirrorCS", {"start": v(11.35, 26.25) * mm, "end": v(4.4, 26.25) * mm});
            skLineSegment(sketch, "E136.MirrorCS", {"start": v(6.1, 31.5) * mm, "end": v(10.64, 26.96) * mm});
            skArc(sketch, "E137.MirrorCS", {"start": v(11.35, 34.28) * mm, "mid": v(10.12, 32.43) * mm, "end": v(7.94, 32.86) * mm});
            skArc(sketch, "E138.MirrorCS", {"start": v(10.64, 26.96) * mm, "mid": v(10.94, 26.25) * mm, "end": v(10.64, 25.54) * mm});
            skLineSegment(sketch, "E139.MirrorCS", {"start": v(4.4, 26.25) * mm, "end": v(4.4, 30.79) * mm});
            skArc(sketch, "E140.MirrorCS", {"start": v(4.4, 30.79) * mm, "mid": v(5.02, 31.7) * mm, "end": v(6.1, 31.5) * mm});
            skPoint(sketch, "E141.MirrorP", {"position": v(4.4, 19.3) * mm});
            skArc(sketch, "E142.MirrorCS", {"start": v(6.1, 21) * mm, "mid": v(5.02, 20.8) * mm, "end": v(4.4, 21.71) * mm});
            skLineSegment(sketch, "E143.MirrorCS", {"start": v(6.1, 21) * mm, "end": v(10.64, 25.54) * mm});
            skLineSegment(sketch, "E144.MirrorCS", {"start": v(4.4, 26.25) * mm, "end": v(4.4, 21.71) * mm});
            skPoint(sketch, "E145.MirrorP", {"position": v(11.35, 26.25) * mm});
            skSolve(sketch);
        }
        {
            var Q0;
            Q0=qSketchRegion(id+"F22",true);
            var Q1;
            {var subQ0=sQuery(id+"F1.wireOp",EDGE,"E37.MirrorCS");var subQ1=makeQuery(id+"F2.opExtrude","SWEPT_FACE",FACE,{"disambiguationData":[OSD([subQ0])]});var subQ2=sQuery(id+"F1.wireOp",EDGE,"E36.MirrorCS");var subQ3=sQuery(id+"F1.wireOp",EDGE,"E35");var subQ4=sQuery(id+"F1.wireOp",EDGE,"E38.MirrorCS");Q1=makeQuery(id+"F8.boolean.opBoolean","SPLIT",FACE,{"disambiguationData":[TD([makeQuery(id+"F2.opExtrude","CAP_FACE",FACE,{"disambiguationData":[OSD([sQuery(id+"F1.wireOp",EDGE,"E24"),sQuery(id+"F1.wireOp",EDGE,"E25"),sQuery(id+"F1.wireOp",EDGE,"E31"),sQuery(id+"F1.wireOp",EDGE,"E32"),sQuery(id+"F1.wireOp",EDGE,"E33"),sQuery(id+"F1.wireOp",EDGE,"E34"),subQ3,subQ2,subQ0,subQ4])],"isStart":true})])],"derivedFrom":subQ1});}
            extrude(context, id + "F23", {"entities" : qUnion([Q0]), "operationType" : NewBodyOperationType.REMOVE, "endBound" : BoundingType.UP_TO_SURFACE, "endBoundEntityFace" : qUnion([Q1]), "depth" : 8 * mm});
        }
        {
            var Q0;
            Q0=makeQuery(id+"F8.boolean.opBoolean","MERGE",FACE,{"derivedFrom":[makeQuery(id+"F2.opExtrude","SWEPT_FACE",FACE,{"disambiguationData":[OSD([sQuery(id+"F1.wireOp",EDGE,"E24"),sQuery(id+"F1.wireOp",EDGE,"E25")])]}),makeQuery(id+"F8.opExtrude","CAP_FACE",FACE,{"disambiguationData":[OSD([sQuery(id+"F7.wireOp",EDGE,"E41"),sQuery(id+"F7.wireOp",EDGE,"E42"),sQuery(id+"F7.wireOp",EDGE,"E44"),sQuery(id+"F7.wireOp",EDGE,"E45.MirrorCS"),sQuery(id+"F7.wireOp",EDGE,"E46.MirrorCS"),sQuery(id+"F7.wireOp",EDGE,"E47.MirrorCS"),sQuery(id+"F7.wireOp",EDGE,"E48.trimOffspring")])],"isStart":true})]});
            var sketch = newSketch(context, id + "F24", { "sketchPlane" : qUnion([Q0])});
            skLineSegment(sketch, "E146", {"start": v(11.35, -16.5) * mm, "end": v(11.35, -9.42) * mm});
            skLineSegment(sketch, "E147.MirrorCS", {"start": v(-11.35, -16.5) * mm, "end": v(-11.35, -9.42) * mm});
            skLineSegment(sketch, "E148", {"start": v(11.35, -16.5) * mm, "end": v(11.35, -12.6) * mm});
            skLineSegment(sketch, "E149", {"start": v(15.25, -4.5) * mm, "end": v(15.25, -12.6) * mm});
            skLineSegment(sketch, "E150.MirrorCS", {"start": v(-15.25, -4.5) * mm, "end": v(-15.25, -12.6) * mm});
            skLineSegment(sketch, "E151", {"start": v(11.35, -12.6) * mm, "end": v(11.35, -9.42) * mm});
            skLineSegment(sketch, "E152", {"start": v(11.35, -16.5) * mm, "end": v(15.25, -12.6) * mm});
            skLineSegment(sketch, "E153", {"start": v(-11.35, -16.5) * mm, "end": v(-15.25, -12.6) * mm});
            skLineSegment(sketch, "E154", {"start": v(11.35, -10.3) * mm, "end": v(15.25, -4.5) * mm});
            skLineSegment(sketch, "E155.MirrorCS", {"start": v(-11.35, -10.3) * mm, "end": v(-15.25, -4.5) * mm});
            skPoint(sketch, "E156.MirrorCS.end.orphan", {"position": v(-15.25, -4.5) * mm});
            skSolve(sketch);
        }
        {
            var Q0;
            Q0=qSketchRegion(id+"F24",true);
            var Q1;
            {var subQ0=sQuery(id+"F1.wireOp",EDGE,"E38.MirrorCS");var subQ1=sQuery(id+"F1.wireOp",EDGE,"E37.MirrorCS");var subQ2=sQuery(id+"F1.wireOp",EDGE,"E36.MirrorCS");var subQ3=sQuery(id+"F1.wireOp",EDGE,"E35");var subQ4=sQuery(id+"F1.wireOp",EDGE,"E34");var subQ5=sQuery(id+"F1.wireOp",EDGE,"E33");var subQ6=sQuery(id+"F1.wireOp",EDGE,"E32");var subQ7=sQuery(id+"F1.wireOp",EDGE,"E31");var subQ8=sQuery(id+"F1.wireOp",EDGE,"E25");var subQ9=sQuery(id+"F1.wireOp",EDGE,"E24");var subQ13=makeQuery(id+"F2.opExtrude","SWEPT_FACE",FACE,{"disambiguationData":[OSD([subQ3,subQ2])]});Q1=makeQuery(id+"F8.boolean.opBoolean","MERGE",FACE,{"derivedFrom":[makeQuery(id+"F5.boolean.opBoolean","SPLIT",FACE,{"disambiguationData":[TD([makeQuery(id+"F2.opExtrude","CAP_FACE",FACE,{"disambiguationData":[OSD([subQ9,subQ8,subQ7,subQ6,subQ5,subQ4,subQ3,subQ2,subQ1,subQ0])],"isStart":true})])],"derivedFrom":subQ13}),makeQuery(id+"F5.boolean.opBoolean","SPLIT",FACE,{"disambiguationData":[TD([makeQuery(id+"F2.opExtrude","CAP_FACE",FACE,{"disambiguationData":[OSD([subQ9,subQ8,subQ7,subQ6,subQ5,subQ4,subQ3,subQ2,subQ1,subQ0])],"isStart":false})])],"derivedFrom":subQ13}),makeQuery(id+"F8.opExtrude","CAP_FACE",FACE,{"disambiguationData":[OSD([sQuery(id+"F7.wireOp",EDGE,"E41"),sQuery(id+"F7.wireOp",EDGE,"E42"),sQuery(id+"F7.wireOp",EDGE,"E44"),sQuery(id+"F7.wireOp",EDGE,"E45.MirrorCS"),sQuery(id+"F7.wireOp",EDGE,"E46.MirrorCS"),sQuery(id+"F7.wireOp",EDGE,"E47.MirrorCS"),sQuery(id+"F7.wireOp",EDGE,"E48.trimOffspring")])],"isStart":false})]});}
            extrude(context, id + "F25", {"entities" : qUnion([Q0]), "operationType" : NewBodyOperationType.ADD, "endBound" : BoundingType.UP_TO_SURFACE, "oppositeDirection" : true, "endBoundEntityFace" : qUnion([Q1]), "depth" : 25 * mm});
        }
        {
            var Q0;
            Q0=makeQuery(id+"F5.boolean.opBoolean","COPY",EDGE,{"derivedFrom":makeQuery(id+"F5.opExtrude","CAP_EDGE",EDGE,{"disambiguationData":[OSD([sQuery(id+"F4.wireOp",EDGE,"E39")])],"isStart":false})});
            fillet(context, id + "F26", {"entities" : qUnion([Q0]), "radius" : 1.5 * mm, "tangentPropagation" : true, "allowEdgeOverflow" : false});
        }
        {
            var Q0;
            Q0=makeQuery(id+"F25.boolean.opBoolean","MERGE",FACE,{"derivedFrom":[makeQuery(id+"F8.boolean.opBoolean","MERGE",FACE,{"derivedFrom":[makeQuery(id+"F2.opExtrude","SWEPT_FACE",FACE,{"disambiguationData":[OSD([sQuery(id+"F1.wireOp",EDGE,"E24"),sQuery(id+"F1.wireOp",EDGE,"E25")])]}),makeQuery(id+"F8.opExtrude","CAP_FACE",FACE,{"disambiguationData":[OSD([sQuery(id+"F7.wireOp",EDGE,"E41"),sQuery(id+"F7.wireOp",EDGE,"E42"),sQuery(id+"F7.wireOp",EDGE,"E44"),sQuery(id+"F7.wireOp",EDGE,"E45.MirrorCS"),sQuery(id+"F7.wireOp",EDGE,"E46.MirrorCS"),sQuery(id+"F7.wireOp",EDGE,"E47.MirrorCS"),sQuery(id+"F7.wireOp",EDGE,"E48.trimOffspring")])],"isStart":true})]}),makeQuery(id+"F25.opExtrude","CAP_FACE",FACE,{"disambiguationData":[OSD([sQuery(id+"F24.wireOp",EDGE,"E148"),sQuery(id+"F24.wireOp",EDGE,"E149"),sQuery(id+"F24.wireOp",EDGE,"E151"),sQuery(id+"F24.wireOp",EDGE,"E152"),sQuery(id+"F24.wireOp",EDGE,"E154")])],"isStart":true}),makeQuery(id+"F25.opExtrude","CAP_FACE",FACE,{"disambiguationData":[OSD([sQuery(id+"F24.wireOp",EDGE,"E150.MirrorCS"),sQuery(id+"F24.wireOp",EDGE,"E147.MirrorCS"),sQuery(id+"F24.wireOp",EDGE,"E153"),sQuery(id+"F24.wireOp",EDGE,"E155.MirrorCS")])],"isStart":true})]});
            var sketch = newSketch(context, id + "F27", { "sketchPlane" : qUnion([Q0])});
            skCircle(sketch, "E157", {"center": v(0, -33.85) * mm, "radius": 4 * mm});
            skPoint(sketch, "E158.end.orphan", {"position": v(0, -29.85) * mm});
            skPoint(sketch, "E159.end.orphan", {"position": v(0, -37.85) * mm});
            skSolve(sketch);
        }
        {
            var Q0;
            Q0=makeQuery(id+"F27.imprint","IMPRINT",FACE,{"disambiguationData":[TD([[makeQuery(id+"F27.imprint","IMPRINT",EDGE,{"derivedFrom":sQuery(id+"F27.wireOp",EDGE,"KxPfJ5i4-knaX-OHmK-AYKn-uu4kdqfgtmBE")}),-1.0]])]});
            var Q1;
            Q1=makeQuery(id+"F27.imprint","IMPRINT",FACE,{"disambiguationData":[TD([[makeQuery(id+"F27.imprint","IMPRINT",EDGE,{"derivedFrom":sQuery(id+"F27.wireOp",EDGE,"E157")}),1.0]])]});
            extrude(context, id + "F28", {"entities" : qUnion([Q0, Q1]), "operationType" : NewBodyOperationType.REMOVE, "oppositeDirection" : true, "depth" : 12 * mm});
        }
    });
